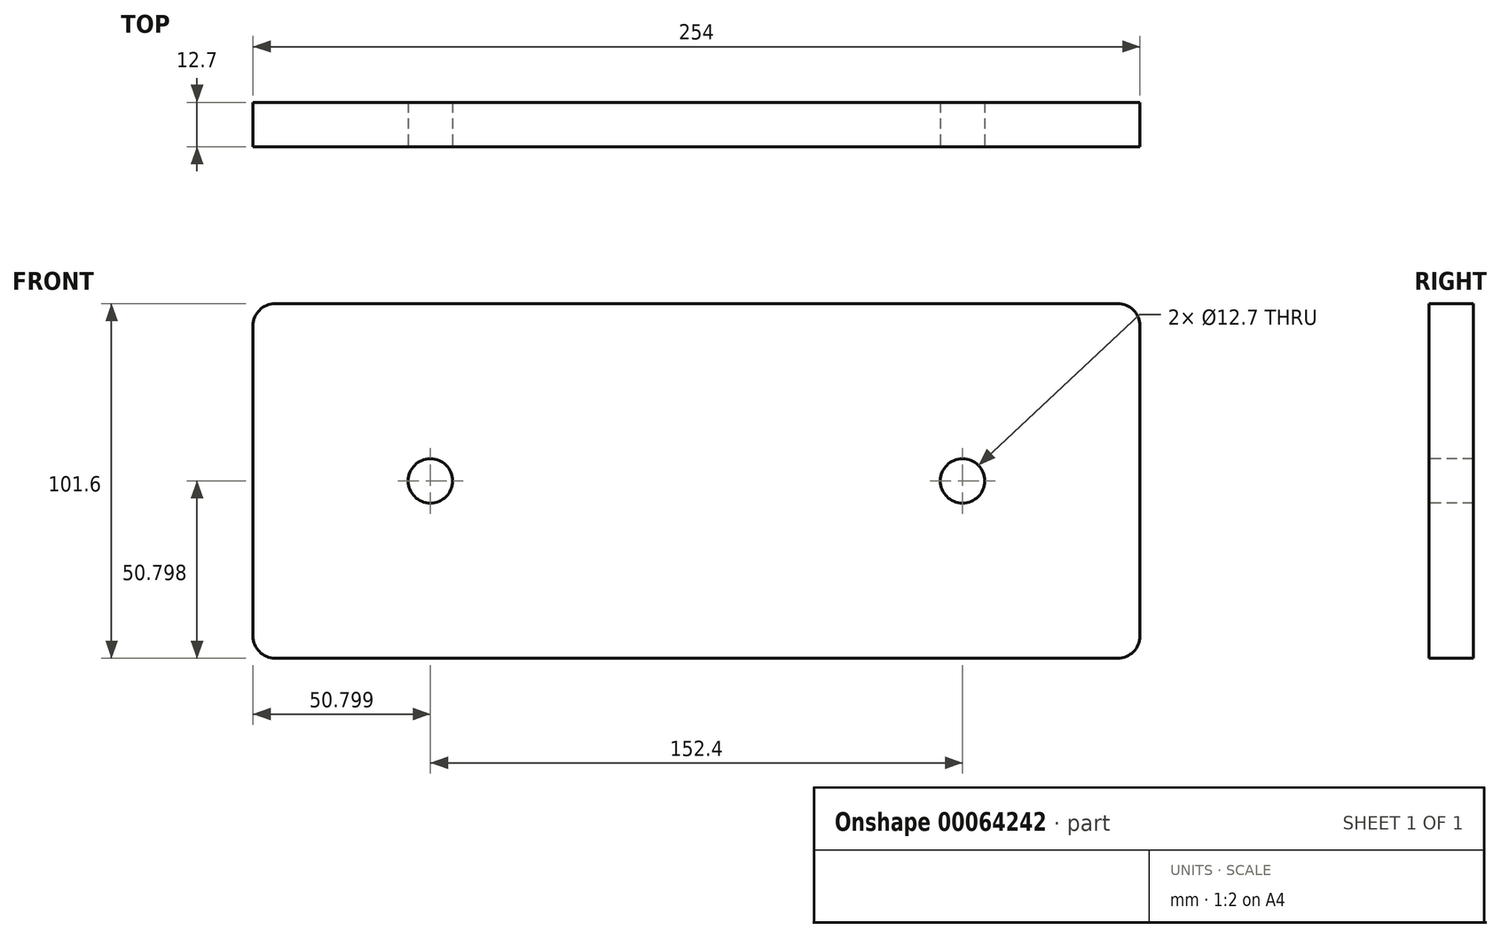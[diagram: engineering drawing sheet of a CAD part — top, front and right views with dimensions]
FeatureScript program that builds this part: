
annotation { "Feature Type Name" : "Feature", "Feature Type Description" : "" }
export const myFeature = defineFeature(function(context is Context, id is Id, definition is map)
    precondition{}
    {
        {
            var Q0;
            Q0=qCreatedBy(makeId("Front.planeOp"),FACE);
            var sketch = newSketch(context, id + "F0", { "sketchPlane" : qUnion([Q0])});
            skLineSegment(sketch, "E0.bottom", {"start": v(-133.14, 39.22) * mm, "end": v(120.86, 39.22) * mm});
            skLineSegment(sketch, "E0.top", {"start": v(-133.14, -62.38) * mm, "end": v(120.86, -62.38) * mm});
            skLineSegment(sketch, "E0.left", {"start": v(-133.14, 39.22) * mm, "end": v(-133.14, -62.38) * mm});
            skLineSegment(sketch, "E0.right", {"start": v(120.86, 39.22) * mm, "end": v(120.86, -62.38) * mm});
            skSolve(sketch);
        }
        {
            var Q0;
            Q0 = qSketchRegion(id + "F0", true);
            extrude(context, id + "F1", {"entities" : qUnion([Q0]), "depth" : 12.7 * mm});
        }
        {
            var Q0;
            Q0=makeQuery(id+"F1.opExtrude","SWEPT_EDGE",EDGE,{"disambiguationData":[OSD([sQuery(id+"F0.wireOp",EDGE,"E0.bottom"),sQuery(id+"F0.wireOp",EDGE,"E0.left")])]});
            var Q1;
            Q1=makeQuery(id+"F1.opExtrude","SWEPT_EDGE",EDGE,{"disambiguationData":[OSD([sQuery(id+"F0.wireOp",EDGE,"E0.bottom"),sQuery(id+"F0.wireOp",EDGE,"E0.right")])]});
            var Q2;
            Q2=makeQuery(id+"F1.opExtrude","SWEPT_EDGE",EDGE,{"disambiguationData":[OSD([sQuery(id+"F0.wireOp",EDGE,"E0.top"),sQuery(id+"F0.wireOp",EDGE,"E0.left")])]});
            var Q3;
            Q3=makeQuery(id+"F1.opExtrude","SWEPT_EDGE",EDGE,{"disambiguationData":[OSD([sQuery(id+"F0.wireOp",EDGE,"E0.top"),sQuery(id+"F0.wireOp",EDGE,"E0.right")])]});
            fillet(context, id + "F2", {"entities" : qUnion([Q0, Q1, Q2, Q3]), "radius" : 6.35 * mm, "tangentPropagation" : true, "allowEdgeOverflow" : false});
        }
        {
            var Q0;
            Q0=makeQuery(id+"F1.opExtrude","CAP_FACE",FACE,{"disambiguationData":[OSD([sQuery(id+"F0.wireOp",EDGE,"E0.bottom"),sQuery(id+"F0.wireOp",EDGE,"E0.top"),sQuery(id+"F0.wireOp",EDGE,"E0.left"),sQuery(id+"F0.wireOp",EDGE,"E0.right")])],"isStart":false});
            var sketch = newSketch(context, id + "F3", { "sketchPlane" : qUnion([Q0])});
            skPoint(sketch, "E1", {"position": v(-82.34, -11.58) * mm});
            skPoint(sketch, "E1.positionSnap0", {"position": v(-133.14, -11.58) * mm});
            skPoint(sketch, "E2", {"position": v(70.06, -11.58) * mm});
            skSolve(sketch);
        }
        {
            var Q0;
            Q0=sQuery(id+"F3.wireOp",VERTEX,"E1");
            var Q1;
            Q1=sQuery(id+"F3.wireOp",VERTEX,"E2");
            var Q2;
            Q2=makeQuery(id+"F1.opExtrude","SWEPT_BODY",BODY,{"disambiguationData":[OSD([sQuery(id+"F0.wireOp",EDGE,"E0.bottom"),sQuery(id+"F0.wireOp",EDGE,"E0.top"),sQuery(id+"F0.wireOp",EDGE,"E0.left"),sQuery(id+"F0.wireOp",EDGE,"E0.right")])]});
            hole(context, id + "F4", {"style" : HoleStyle.SIMPLE, "holeDiameter" : 12.7 * mm, "endStyle" : HoleEndStyle.THROUGH, "locations" : qUnion([Q0, Q1]), "scope" : qUnion([Q2])});
        }
    });
